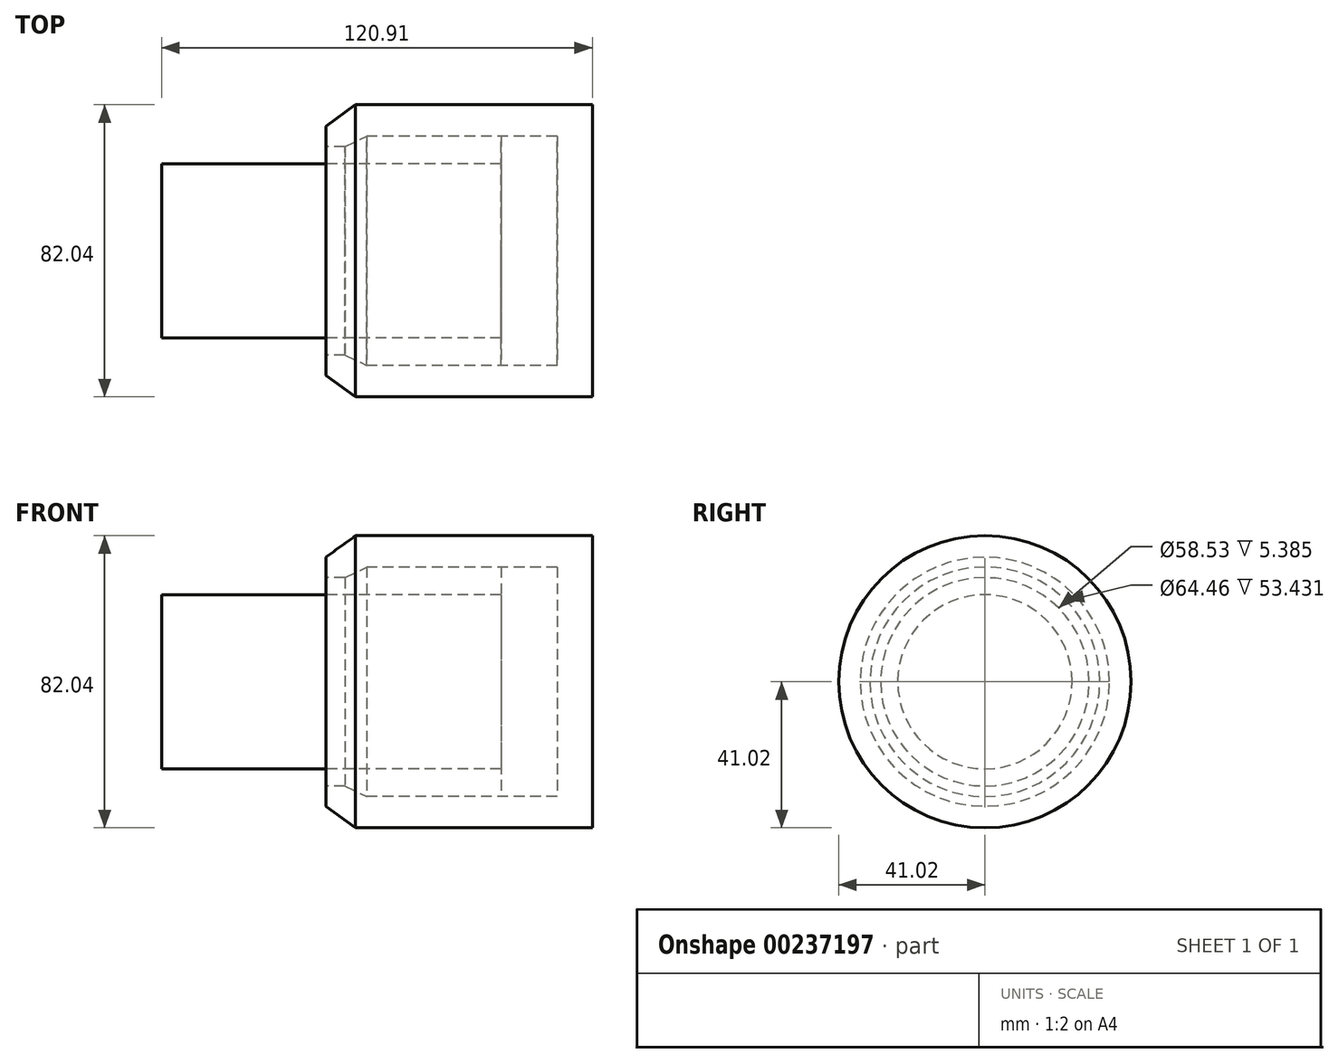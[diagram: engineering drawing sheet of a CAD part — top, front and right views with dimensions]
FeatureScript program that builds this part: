
annotation { "Feature Type Name" : "Feature", "Feature Type Description" : "" }
export const myFeature = defineFeature(function(context is Context, id is Id, definition is map)
    precondition{}
    {
        {
            var Q0;
            Q0=qCreatedBy(makeId("Front.planeOp"),FACE);
            var sketch = newSketch(context, id + "F0", { "sketchPlane" : qUnion([Q0])});
            skLineSegment(sketch, "E0", {"start": v(-118.06, 0) * mm, "end": v(118.06, 0) * mm, "construction": true});
            skLineSegment(sketch, "E1", {"start": v(0, 0) * mm, "end": v(0, 24.47) * mm});
            skPoint(sketch, "E1.endSnap0", {"position": v(0, 0) * mm});
            skLineSegment(sketch, "E2", {"start": v(0, 24.47) * mm, "end": v(95.25, 24.47) * mm});
            skLineSegment(sketch, "E3", {"start": v(95.25, 24.47) * mm, "end": v(95.25, 32.23) * mm});
            skLineSegment(sketch, "E4", {"start": v(95.25, 32.23) * mm, "end": v(111.04, 32.23) * mm});
            skLineSegment(sketch, "E5", {"start": v(111.04, 32.23) * mm, "end": v(111.04, 0) * mm});
            skLineSegment(sketch, "E6", {"start": v(0, 0) * mm, "end": v(111.04, 0) * mm});
            skSolve(sketch);
        }
        {
            var Q0;
            Q0 = qSketchRegion(id + "F0", true);
            var Q1;
            Q1=sQuery(id+"F0.wireOp",EDGE,"E0");
            revolve(context, id + "F1", {"entities" : qUnion([Q0]), "axis" : qUnion([Q1]), "revolveType" : RevolveType.FULL});
        }
        {
            var Q0;
            Q0=qCreatedBy(makeId("Front.planeOp"),FACE);
            var sketch = newSketch(context, id + "F2", { "sketchPlane" : qUnion([Q0])});
            skLineSegment(sketch, "E7", {"start": v(111.04, 0) * mm, "end": v(111.04, 32.23) * mm});
            skLineSegment(sketch, "E8", {"start": v(111.04, 32.23) * mm, "end": v(57.6, 32.23) * mm});
            skLineSegment(sketch, "E9", {"start": v(57.6, 32.23) * mm, "end": v(51.45, 29.26) * mm});
            skLineSegment(sketch, "E10", {"start": v(51.45, 29.26) * mm, "end": v(46.07, 29.26) * mm});
            skLineSegment(sketch, "E11", {"start": v(46.07, 29.26) * mm, "end": v(46.07, 34.98) * mm});
            skLineSegment(sketch, "E12", {"start": v(46.07, 34.98) * mm, "end": v(54.42, 41.02) * mm});
            skLineSegment(sketch, "E13", {"start": v(54.42, 41.02) * mm, "end": v(120.91, 41.02) * mm});
            skLineSegment(sketch, "E14", {"start": v(120.91, 41.02) * mm, "end": v(120.91, 0) * mm});
            skLineSegment(sketch, "E15", {"start": v(120.91, 0) * mm, "end": v(111.04, 0) * mm});
            skSolve(sketch);
        }
        {
            var Q0;
            Q0 = qSketchRegion(id + "F2", true);
            var Q1;
            Q1=sQuery(id+"F0.wireOp",EDGE,"E0");
            revolve(context, id + "F3", {"entities" : qUnion([Q0]), "axis" : qUnion([Q1]), "revolveType" : RevolveType.FULL});
        }
    });
